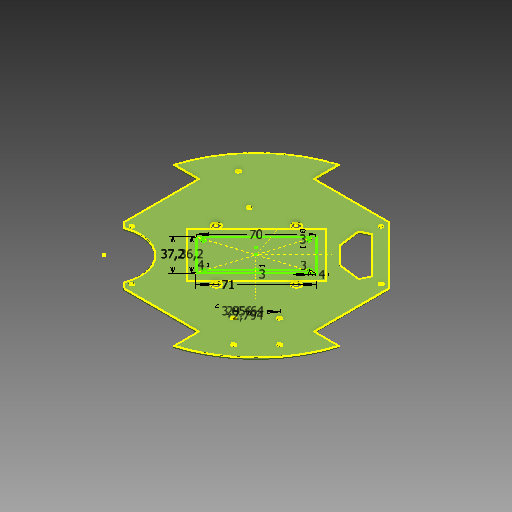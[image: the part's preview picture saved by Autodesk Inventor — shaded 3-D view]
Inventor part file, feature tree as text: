
AUTODESK INVENTOR PART (.ipt)
format: ipt  version: 2020 (Build 240168000, 168)  size: 300,032 bytes
history: native  units: mm
features: sketch x7, extrude x5, other x2, hole x1, projected_geometry x1
ambient origin geometry x8: Origin, YZ Plane, XZ Plane, XY Plane, X Axis, Y Axis, Z Axis, Center Point
bodies: Body1 (feature_tree)
feature tree (16):
  other  "Board1.2"
  other  "Твердое тело1"
  extrude  "Выдавливание1"  Depth=3.055801mm
  sketch  "Эскиз2"
  extrude  "Выдавливание4"  Depth=29.464mm
  extrude  "Выдавливание5"  Depth=2.794mm
  extrude  "Выдавливание6"  TaperAngle=0.0deg  [1 undecoded]
  sketch  "Эскиз7"
  extrude  "Выдавливание8"  TaperAngle=0.0deg  [1 undecoded]
  hole  "Отверстие1"  [1 undecoded]
  sketch  "Эскиз8"
  sketch  "Эскиз1"
  sketch  "Эскиз4"
  sketch  "Эскиз5"
  sketch  "Эскиз6"
  projected_geometry  "Спроецированная петля1"
note: 3 required parameter values undecoded (feature->parameter linkage not recoverable at this tier; creation-order binding heuristic only, values carry confidence <= 0.55)
